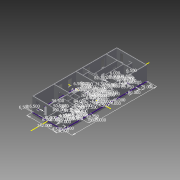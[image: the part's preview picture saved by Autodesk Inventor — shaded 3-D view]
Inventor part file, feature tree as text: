
AUTODESK INVENTOR PART (.ipt)
format: ipt  version: 2013 SP2 (Build 170200200, 200)  size: 778,240 bytes
history: native  units: in
note: dims shown in document units (in); Inventor stores cm internally (conversion verified against a paired STEP export)
features: extrude x17, sketch x8, projected_geometry x6
ambient origin geometry x8: Origin, YZ Plane, XZ Plane, XY Plane, X Axis, Y Axis, Z Axis, Center Point
bodies: Solid1 (feature_tree)
feature tree (31):
  sketch  "Sketch1"  dims[d0=675.0in d2=242.0in]
  extrude  "Extrusion1"  Depth=242.0in
  extrude  "Extrusion2"  Depth=4.5in
  extrude  "Extrusion3"  Depth=6.5in
  extrude  "Extrusion4"  Depth=6.0in
  sketch  "Sketch3"  dims[d12=4.5in d13=173.75in d14=6.5in d15=6.5in]
  extrude  "Extrusion13"  Depth=4.5in
  extrude  "Extrusion12"  Depth=4.5in
  extrude  "Extrusion11"  Depth=4.5in
  extrude  "Extrusion10"  Depth=6.0in
  extrude  "Extrusion9"  Depth=4.5in
  extrude  "Extrusion14"  Depth=6.5in
  extrude  "Extrusion15"  Depth=4.5in
  extrude  "Extrusion16"  Depth=4.5in
  extrude  "Extrusion17"  Depth=47.5in
  extrude  "Extrusion5"  Depth=6.5in
  extrude  "Extrusion6"  Depth=6.5in
  extrude  "Extrusion7"  Depth=84.0in
  extrude  "Extrusion8"  Depth=82.0in
  sketch  "Sketch2"  dims[d3=666.0in d4=233.0in d5=4.5in d7=96.75in]
  projected_geometry  "Projected Loop1"
  projected_geometry  "Projected Loop2"
  sketch  "Sketch4"  dims[d16=4.5in d17=176.5in d22=6.0in]
  projected_geometry  "Projected Loop3"
  projected_geometry  "Projected Loop4"
  projected_geometry  "Projected Loop5"
  sketch  "Sketch5"  dims[d23=4.5in d25=4.5in]
  sketch  "Sketch6"  dims[d30=4.5in d33=4.5in d35=6.0in]
  sketch  "Sketch7"  dims[d36=4.5in d38=4.5in]
  sketch  "Sketch8"  dims[d41=4.5in d42=6.0in d44=4.5in d45=6.5in d48=4.5in d54=4.5in d56=47.5in d64=6.5in d66=6.5in d67=84.0in d70=82.0in d71=4.5in d73=116.0in d74=4.5in d76=36.0in d79=91.5in d80=34.5in d81=62.5in d82=26.75in d83=4.5in d92=80.0in d93=6.0in d95=36.0in d96=6.0in d99=8.0in d100=8.0in d112=1.5in d113=29.75in d117=33.0in d125=4.5in d126=6.0in d128=36.0in d133=4.5in d134=4.5in d135=18.0in d136=12.0in d137=6.0in d138=50.5in d139=16.75in d140=4.5in d141=4.5in d145=160.0in d146=34.5in d147=39.75in d149=22.5in d150=98.0in d152=4.5in d154=119.5in d155=84.0in d159=15.5in d160=91.5in d161=4.5in d162=4.5in d163=4.5in d164=4.5in d165=76.0in d166=79.0in d168=112.5in d173=6.5in d174=36.5in d175=40.0in d176=24.0in d177=4.5in d178=41.0in d179=66.0in d180=8.0in d181=28.0in d182=47.5in d183=4.5in d184=4.5in d185=82.75in d187=3.0in d188=31.5in d189=80.0in d190=18.0in d191=42.0in d192=31.5in d193=47.5in d194=82.75in d195=18.0in d196=2.0in d197=4.0in d198=2.0in d199=24.0in d200=91.5in d201=4.5in d203=4.5in d204=29.75in d205=84.0in d206=4.5in d207=6.5in d208=31.5in d209=38.0in d210=4.5in d211=4.5in d212=24.0in d213=9.75in d214=8.75in d215=8.75in d216=98.0in d217=4.5in d218=36.5in d219=6.0in d220=84.0in d221=24.0in d222=21.0in d223=4.5in d224=4.5in d225=112.5in d226=6.0in d227=4.0in d228=29.75in d229=4.5in d230=89.75in d231=15.5in d232=12.0in d233=4.5in d234=4.5in d235=23.5in d236=112.0in d237=0.0in d238=112.0in d239=0.0in d240=112.0in d241=0.0in d242=46.0in d244=18.25in d245=0.0in d247=12.0in d249=17.25in d250=0.0in d251=11.25in d252=0.0in d253=17.25in d254=0.0in d255=0.01in d256=0.0in d257=6.0in d258=32.5in d259=0.0in d260=31.5in d261=0.0in d262=33.5in d263=0.0in d264=30.0in d265=0.0in d266=32.5in d267=0.0in d268=63.0in d270=31.0in d271=26.25in d272=26.25in d274=60.0in d276=12.0in d277=26.25in d279=32.5in d280=0.0in d281=26.25in d284=6.0in d285=31.0in d286=63.0in d287=26.25in d288=63.0in d289=36.0in d290=31.0in d291=26.25in d292=63.0in d293=0.625in d294=31.0in d295=26.25in d296=63.0in d297=4.625in d298=31.0in d299=32.5in d300=0.0in d301=44.0in d302=31.0in d303=63.0in d304=26.25in d305=32.5in d306=0.0in d307=12.0in d308=28.0in d309=49.0in d311=30.75in d312=33.75in d313=53.0in d314=31.0in d315=31.0in d316=31.0in d317=26.25in d318=63.0in d319=26.25in d320=32.5in d321=0.0in d322=205.9055in]
  projected_geometry  "Projected Loop6"
